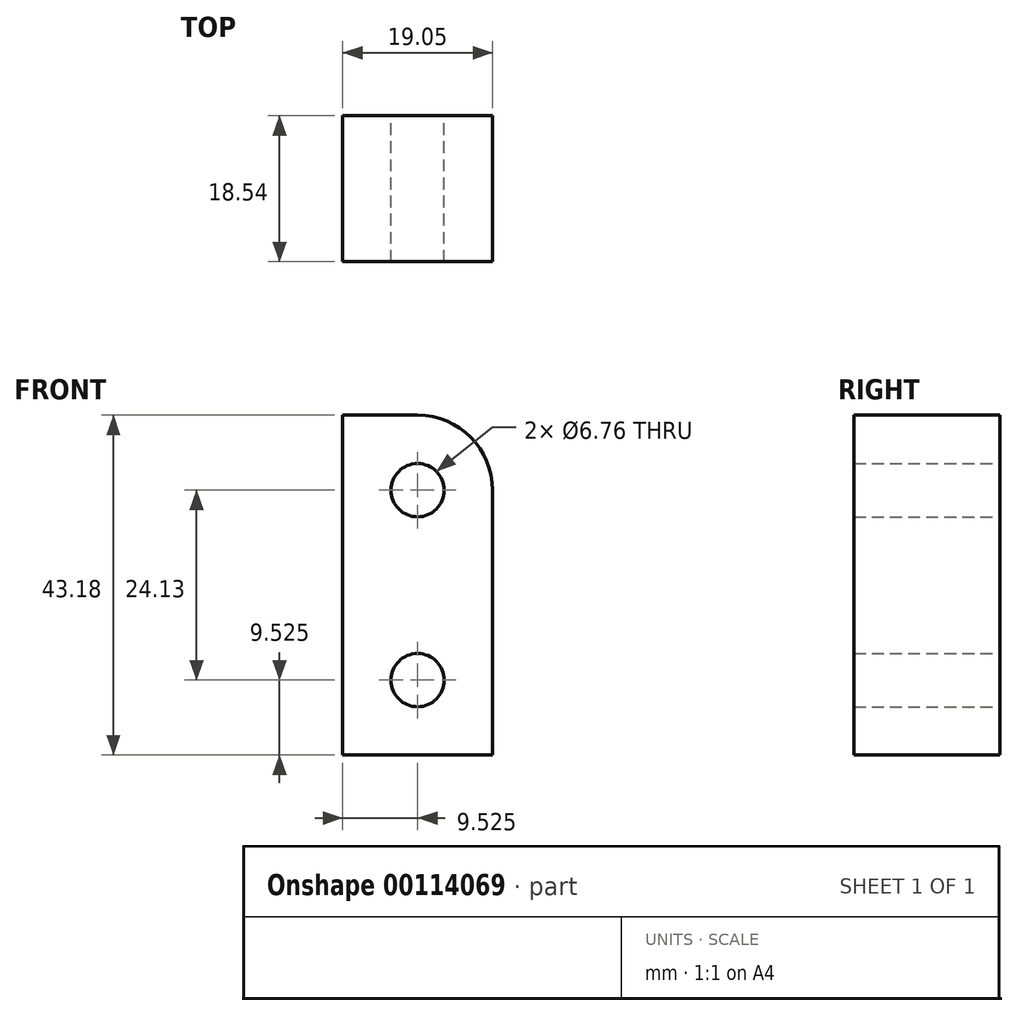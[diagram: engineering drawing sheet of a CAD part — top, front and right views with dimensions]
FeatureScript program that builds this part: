
annotation { "Feature Type Name" : "Feature", "Feature Type Description" : "" }
export const myFeature = defineFeature(function(context is Context, id is Id, definition is map)
    precondition{}
    {
        {
            var Q0;
            Q0=qCreatedBy(makeId("Front.planeOp"),FACE);
            var sketch = newSketch(context, id + "F0", { "sketchPlane" : qUnion([Q0])});
            skLineSegment(sketch, "E0.bottom", {"start": v(0, 0) * mm, "end": v(19.05, 0) * mm});
            skLineSegment(sketch, "E0.top", {"start": v(0, 43.18) * mm, "end": v(19.05, 43.18) * mm});
            skLineSegment(sketch, "E0.left", {"start": v(0, 0) * mm, "end": v(0, 43.18) * mm});
            skLineSegment(sketch, "E0.right", {"start": v(19.05, 0) * mm, "end": v(19.05, 43.18) * mm});
            skSolve(sketch);
        }
        {
            var Q0;
            Q0 = qSketchRegion(id + "F0", true);
            extrude(context, id + "F1", {"entities" : qUnion([Q0]), "depth" : 18.54 * mm});
        }
        {
            var Q0;
            Q0=makeQuery(id+"F1.opExtrude","SWEPT_EDGE",EDGE,{"disambiguationData":[OSD([sQuery(id+"F0.wireOp",EDGE,"E0.top"),sQuery(id+"F0.wireOp",EDGE,"E0.right")])]});
            fillet(context, id + "F2", {"entities" : qUnion([Q0]), "radius" : 9.52 * mm, "tangentPropagation" : true, "allowEdgeOverflow" : false});
        }
        {
            var Q0;
            Q0=makeQuery(id+"F1.opExtrude","CAP_FACE",FACE,{"disambiguationData":[OSD([sQuery(id+"F0.wireOp",EDGE,"E0.bottom"),sQuery(id+"F0.wireOp",EDGE,"E0.top"),sQuery(id+"F0.wireOp",EDGE,"E0.left"),sQuery(id+"F0.wireOp",EDGE,"E0.right")])],"isStart":false});
            var sketch = newSketch(context, id + "F3", { "sketchPlane" : qUnion([Q0])});
            skLineSegment(sketch, "E1", {"start": v(9.52, 43.18) * mm, "end": v(9.52, 0) * mm, "construction": true});
            skPoint(sketch, "E2", {"position": v(9.52, 33.65) * mm});
            skPoint(sketch, "E3", {"position": v(9.52, 9.53) * mm});
            skSolve(sketch);
        }
        {
            var Q0;
            Q0=sQuery(id+"F3.wireOp",VERTEX,"E2");
            var Q1;
            Q1=sQuery(id+"F3.wireOp",VERTEX,"E3");
            var Q2;
            Q2=makeQuery(id+"F1.opExtrude","SWEPT_BODY",BODY,{"disambiguationData":[OSD([sQuery(id+"F0.wireOp",EDGE,"E0.bottom"),sQuery(id+"F0.wireOp",EDGE,"E0.top"),sQuery(id+"F0.wireOp",EDGE,"E0.left"),sQuery(id+"F0.wireOp",EDGE,"E0.right")])]});
            hole(context, id + "F4", {"style" : HoleStyle.SIMPLE, "endStyle" : HoleEndStyle.THROUGH, "standardTappedOrClearance" : lookupTablePath({ "standard" : "ANSI", "fit" : "Normal (ASME)", "size" : "1/4", "type" : "Clearance" }), "standardBlindInLast" : lookupTablePath({ "fit" : "Free", "standard" : "ANSI", "size" : "1/4", "type" : "Clearance" }), "holeDiameter" : 6.76 * mm, "locations" : qUnion([Q0, Q1]), "scope" : qUnion([Q2]), "isTappedThrough" : true});
        }
    });
